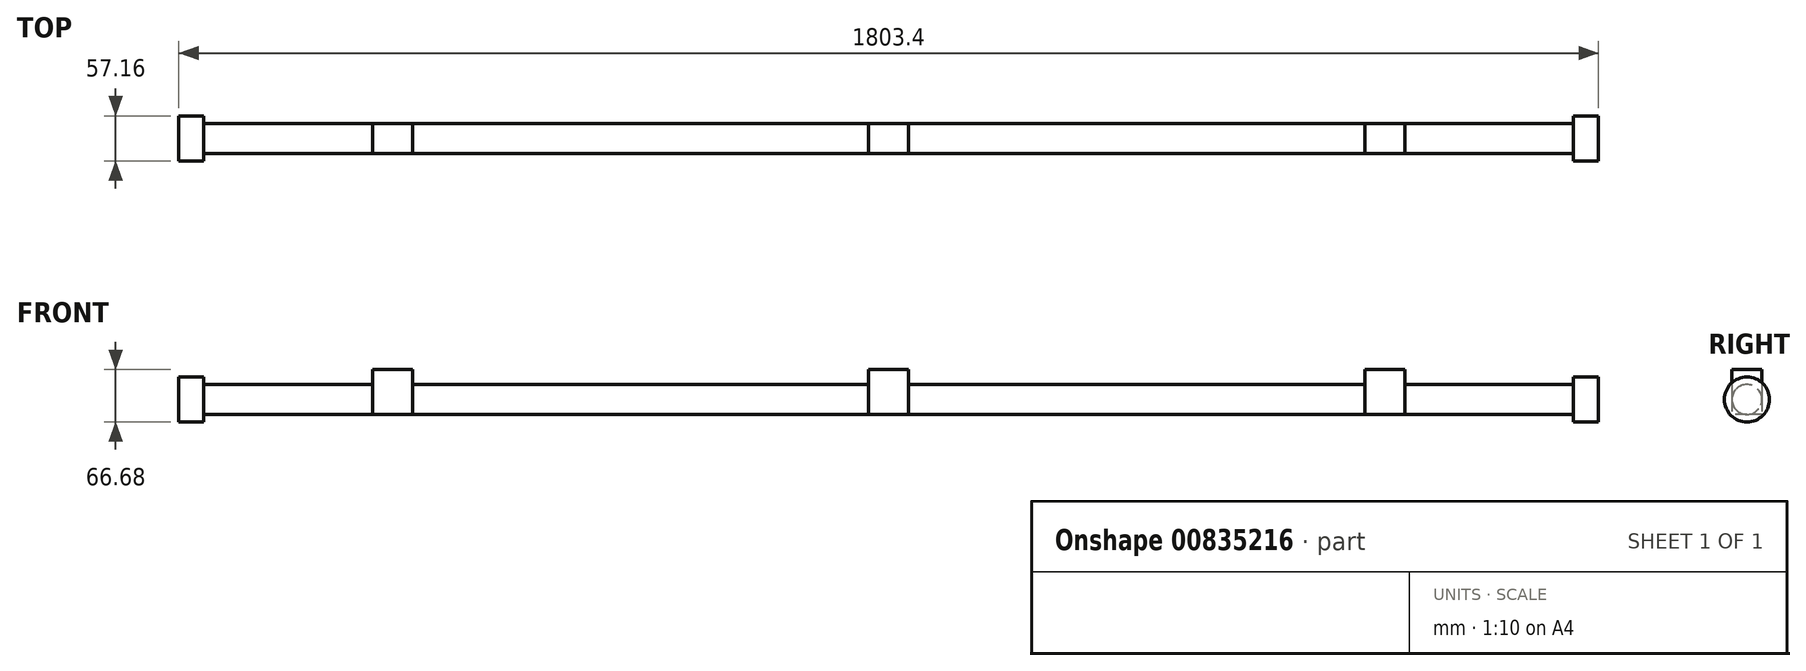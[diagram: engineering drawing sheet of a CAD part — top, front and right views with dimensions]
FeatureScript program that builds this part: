
annotation { "Feature Type Name" : "Feature", "Feature Type Description" : "" }
export const myFeature = defineFeature(function(context is Context, id is Id, definition is map)
    precondition{}
    {
        {
            var Q0;
            Q0=qCreatedBy(makeId("Right.planeOp"),FACE);
            var sketch = newSketch(context, id + "F0", { "sketchPlane" : qUnion([Q0])});
            skCircle(sketch, "E0", {"center": v(0, 0) * mm, "radius": 19.05 * mm});
            skSolve(sketch);
        }
        {
            var Q0;
            Q0 = qSketchRegion(id + "F0", true);
            extrude(context, id + "F1", {"entities" : qUnion([Q0]), "endBound" : BoundingType.SYMMETRIC, "depth" : 1803.4 * mm, "offsetDistance" : 25.4 * mm});
        }
        {
            var Q0;
            Q0=qCreatedBy(makeId("Right.planeOp"),FACE);
            var sketch = newSketch(context, id + "F2", { "sketchPlane" : qUnion([Q0])});
            skLineSegment(sketch, "E1.bottom", {"start": v(19.05, 38.1) * mm, "end": v(-19.05, 38.1) * mm});
            skLineSegment(sketch, "E1.left", {"start": v(19.05, 38.1) * mm, "end": v(19.05, -19.05) * mm});
            skLineSegment(sketch, "E1.right", {"start": v(-19.05, 38.1) * mm, "end": v(-19.05, -19.05) * mm});
            skPoint(sketch, "E1.middle", {"position": v(0, 0) * mm});
            skLineSegment(sketch, "E2", {"start": v(19.05, -19.05) * mm, "end": v(-19.05, -19.05) * mm});
            skSolve(sketch);
        }
        {
            var Q0;
            Q0 = qSketchRegion(id + "F2", true);
            extrude(context, id + "F3", {"entities" : qUnion([Q0]), "operationType" : NewBodyOperationType.ADD, "endBound" : BoundingType.SYMMETRIC, "depth" : 50.8 * mm, "offsetDistance" : 25.4 * mm});
        }
        {
            var Q0;
            Q0=qCreatedBy(makeId("Right.planeOp"),FACE);
            cPlane(context, id + "F4", {"entities" : qUnion([Q0]), "cplaneType" : CPlaneType.OFFSET, "offset" : 630.24 * mm, "width" : 152.4 * mm, "height" : 152.4 * mm});
        }
        {
            var Q0;
            Q0=qCreatedBy(id+"F4.planeOp",FACE);
            var sketch = newSketch(context, id + "F5", { "sketchPlane" : qUnion([Q0])});
            skLineSegment(sketch, "E3.bottom", {"start": v(-19.05, 38.1) * mm, "end": v(19.05, 38.1) * mm});
            skLineSegment(sketch, "E3.top", {"start": v(-19.05, -19.05) * mm, "end": v(19.05, -19.05) * mm});
            skLineSegment(sketch, "E3.left", {"start": v(-19.05, 38.1) * mm, "end": v(-19.05, -19.05) * mm});
            skLineSegment(sketch, "E3.right", {"start": v(19.05, 38.1) * mm, "end": v(19.05, -19.05) * mm});
            skSolve(sketch);
        }
        {
            var Q0;
            Q0 = qSketchRegion(id + "F5", true);
            extrude(context, id + "F6", {"entities" : qUnion([Q0]), "operationType" : NewBodyOperationType.ADD, "endBound" : BoundingType.SYMMETRIC, "depth" : 50.8 * mm, "offsetDistance" : 25.4 * mm});
        }
        {
            var Q0;
            Q0=makeQuery(id+"F1.opExtrude","CAP_FACE",FACE,{"disambiguationData":[OSD([sQuery(id+"F0.wireOp",EDGE,"E0")])],"isStart":false});
            var sketch = newSketch(context, id + "F7", { "sketchPlane" : qUnion([Q0])});
            skCircle(sketch, "E4", {"center": v(0, 0) * mm, "radius": 28.58 * mm});
            skCircle(sketch, "E5", {"center": v(0, 0) * mm, "radius": 19.05 * mm});
            skSolve(sketch);
        }
        {
            var Q0;
            Q0 = qSketchRegion(id + "F7", true);
            extrude(context, id + "F8", {"entities" : qUnion([Q0]), "oppositeDirection" : true, "depth" : 31.75 * mm, "offsetDistance" : 25.4 * mm});
        }
        {
            var Q0;
            Q0=makeQuery(id+"F1.opExtrude","SWEPT_BODY",BODY,{"disambiguationData":[OSD([sQuery(id+"F0.wireOp",EDGE,"E0")])]});
            var Q1;
            Q1=makeQuery(id+"F8.opExtrude","SWEPT_BODY",BODY,{"disambiguationData":[OSD([sQuery(id+"F7.wireOp",EDGE,"E4"),sQuery(id+"F7.wireOp",EDGE,"E5")])]});
            var Q2;
            Q2=qCreatedBy(makeId("Right.planeOp"),FACE);
            mirror(context, id + "F9", {"operationType" : NewBodyOperationType.ADD, "entities" : qUnion([Q0, Q1]), "mirrorPlane" : qUnion([Q2])});
        }
    });
